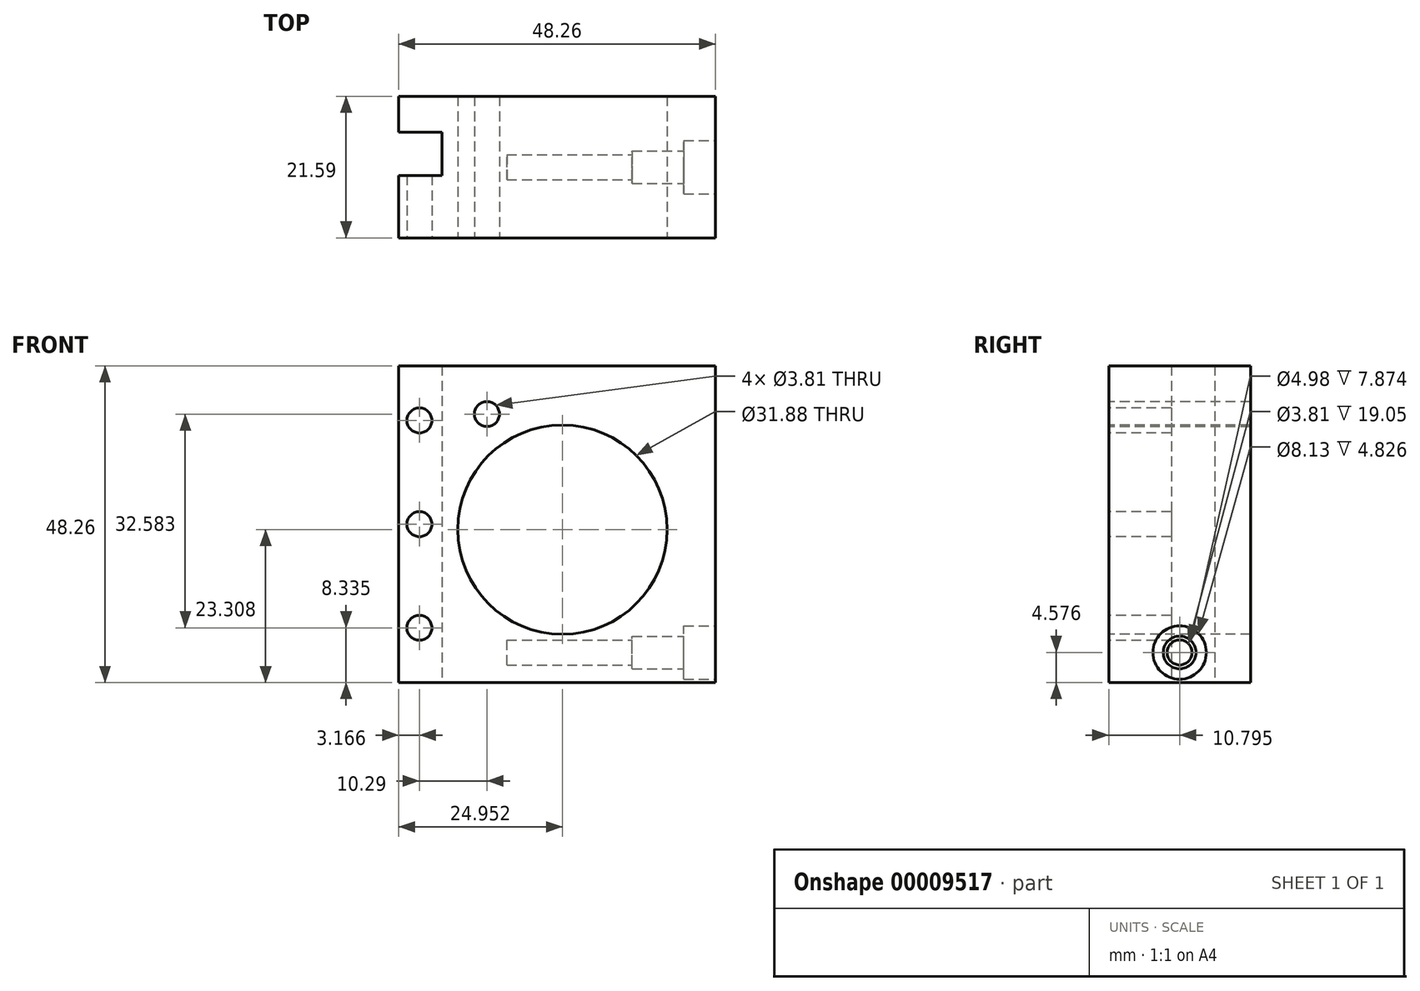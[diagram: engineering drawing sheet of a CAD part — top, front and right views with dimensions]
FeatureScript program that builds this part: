
annotation { "Feature Type Name" : "Feature", "Feature Type Description" : "" }
export const myFeature = defineFeature(function(context is Context, id is Id, definition is map)
    precondition{}
    {
        {
            var Q0;
            Q0=qCreatedBy(makeId("Front.planeOp"),FACE);
            var sketch = newSketch(context, id + "F0", { "sketchPlane" : qUnion([Q0])});
            skLineSegment(sketch, "E0.bottom", {"start": v(-180.25, 28.04) * mm, "end": v(-132, 28.04) * mm});
            skLineSegment(sketch, "E0.top", {"start": v(-180.25, -20.22) * mm, "end": v(-149.6, -20.22) * mm});
            skLineSegment(sketch, "E0.left", {"start": v(-180.25, 28.04) * mm, "end": v(-180.25, -20.22) * mm});
            skLineSegment(sketch, "E0.right", {"start": v(-132, 28.04) * mm, "end": v(-132, -20.22) * mm});
            skCircle(sketch, "E1", {"center": v(-155.3, 3.09) * mm, "radius": 15.94 * mm});
            skLineSegment(sketch, "E2", {"start": v(-155.3, 3.09) * mm, "end": v(-130.34, 3.09) * mm, "construction": true});
            skLineSegment(sketch, "E3", {"start": v(-155.3, 3.09) * mm, "end": v(-155.3, -21.87) * mm, "construction": true});
            skLineSegment(sketch, "E4", {"start": v(-173.65, -20.22) * mm, "end": v(-173.65, 28.04) * mm, "construction": true});
            skLineSegment(sketch, "E5", {"start": v(-177.08, 28.04) * mm, "end": v(-177.08, -20.22) * mm, "construction": true});
            skCircle(sketch, "E6", {"center": v(-177.08, 19.73) * mm, "radius": 1.9 * mm});
            skCircle(sketch, "E7", {"center": v(-177.08, 3.91) * mm, "radius": 1.9 * mm});
            skCircle(sketch, "E8", {"center": v(-177.08, -11.89) * mm, "radius": 1.9 * mm});
            skCircle(sketch, "E9", {"center": v(-166.8, 20.7) * mm, "radius": 1.9 * mm});
            skCircle(sketch, "E10", {"center": v(-155.3, 3.09) * mm, "radius": 4.97 * mm});
            skCircle(sketch, "E11", {"center": v(-155.3, 3.09) * mm, "radius": 7.14 * mm});
            skLineSegment(sketch, "E12.trimOffspring", {"start": v(-146.3, -20.22) * mm, "end": v(-132, -20.22) * mm});
            skCircle(sketch, "E13", {"center": v(-166.8, 20.7) * mm, "radius": 2.45 * mm});
            skLineSegment(sketch, "E14", {"start": v(-149.6, -20.22) * mm, "end": v(-146.3, -20.22) * mm});
            skSolve(sketch);
        }
        {
            var Q0;
            Q0=makeQuery(id+"F0.imprint","IMPRINT",FACE,{"disambiguationData":[TD([[makeQuery(id+"F0.imprint","IMPRINT",EDGE,{"derivedFrom":sQuery(id+"F0.wireOp",EDGE,"E0.bottom")}),-1.0]])]});
            var Q1;
            Q1=makeQuery(id+"F0.imprint","IMPRINT",FACE,{"disambiguationData":[TD([[makeQuery(id+"F0.imprint","IMPRINT",EDGE,{"derivedFrom":sQuery(id+"F0.wireOp",EDGE,"E9")}),1.0]])]});
            var Q2;
            Q2=makeQuery(id+"F0.imprint","IMPRINT",FACE,{"disambiguationData":[TD([[makeQuery(id+"F0.imprint","IMPRINT",EDGE,{"derivedFrom":sQuery(id+"F0.wireOp",EDGE,"E6")}),1.0]])]});
            var Q3;
            Q3=makeQuery(id+"F0.imprint","IMPRINT",FACE,{"disambiguationData":[TD([[makeQuery(id+"F0.imprint","IMPRINT",EDGE,{"derivedFrom":sQuery(id+"F0.wireOp",EDGE,"E7")}),1.0]])]});
            var Q4;
            Q4=makeQuery(id+"F0.imprint","IMPRINT",FACE,{"disambiguationData":[TD([[makeQuery(id+"F0.imprint","IMPRINT",EDGE,{"derivedFrom":sQuery(id+"F0.wireOp",EDGE,"E8")}),1.0]])]});
            var Q5;
            Q5=makeQuery(id+"F0.imprint","IMPRINT",FACE,{"disambiguationData":[TD([[makeQuery(id+"F0.imprint","IMPRINT",EDGE,{"derivedFrom":sQuery(id+"F0.wireOp",EDGE,"E9")}),-1.0]])]});
            var Q6;
            {var subQ1=sQuery(id+"F0.wireOp",EDGE,"2551a94f-3a1d-4b0e-8204-0523b05fb9c7");Q6=makeQuery(id+"F0.imprint","IMPRINT",FACE,{"disambiguationData":[TD([[makeQuery(id+"F0.imprint","IMPRINT",EDGE,{"derivedFrom":subQ1}),1.0]])]});}
            extrude(context, id + "F1", {"entities" : qUnion([Q0, Q1, Q2, Q3, Q4, Q5, Q6]), "oppositeDirection" : true, "depth" : 21.59 * mm});
        }
        {
            var Q0;
            Q0=makeQuery(id+"F0.imprint","IMPRINT",FACE,{"disambiguationData":[TD([[makeQuery(id+"F0.imprint","IMPRINT",EDGE,{"derivedFrom":sQuery(id+"F0.wireOp",EDGE,"E11")}),-1.0]])]});
            var Q1;
            Q1=makeQuery(id+"F0.imprint","IMPRINT",FACE,{"disambiguationData":[TD([[makeQuery(id+"F0.imprint","IMPRINT",EDGE,{"derivedFrom":sQuery(id+"F0.wireOp",EDGE,"E10")}),-1.0]])]});
            var Q2;
            Q2=makeQuery(id+"F0.imprint","IMPRINT",FACE,{"disambiguationData":[TD([[makeQuery(id+"F0.imprint","IMPRINT",EDGE,{"derivedFrom":sQuery(id+"F0.wireOp",EDGE,"E10")}),1.0]])]});
            extrude(context, id + "F2", {"entities" : qUnion([Q0, Q1, Q2]), "oppositeDirection" : true, "depth" : 41.4 * mm});
        }
        {
            var Q0;
            Q0=makeQuery(id+"F0.imprint","IMPRINT",FACE,{"disambiguationData":[TD([[makeQuery(id+"F0.imprint","IMPRINT",EDGE,{"derivedFrom":sQuery(id+"F0.wireOp",EDGE,"E10")}),1.0]])]});
            extrude(context, id + "F3", {"entities" : qUnion([Q0]), "operationType" : NewBodyOperationType.REMOVE, "endBound" : BoundingType.UP_TO_NEXT, "oppositeDirection" : true, "depth" : 25.4 * mm});
        }
        {
            var Q0;
            Q0=makeQuery(id+"F0.imprint","IMPRINT",FACE,{"disambiguationData":[TD([[makeQuery(id+"F0.imprint","IMPRINT",EDGE,{"derivedFrom":sQuery(id+"F0.wireOp",EDGE,"E10")}),-1.0]])]});
            extrude(context, id + "F4", {"entities" : qUnion([Q0]), "operationType" : NewBodyOperationType.REMOVE, "oppositeDirection" : true, "depth" : 3 / 203.2 * mm});
        }
        {
            var Q0;
            Q0=makeQuery(id+"F1.opExtrude","SWEPT_FACE",FACE,{"disambiguationData":[OSD([sQuery(id+"F0.wireOp",EDGE,"E0.top")])]});
            var sketch = newSketch(context, id + "F5", { "sketchPlane" : qUnion([Q0])});
            skLineSegment(sketch, "E15.0", {"start": v(-180.25, -21.59) * mm, "end": v(-180.25, -16.13) * mm, "construction": true});
            skLineSegment(sketch, "E16.0", {"start": v(-180.25, 0) * mm, "end": v(-149.6, 0) * mm, "construction": true});
            skLineSegment(sketch, "E17.0", {"start": v(-180.25, -21.59) * mm, "end": v(-180.25, -21.59) * mm});
            skLineSegment(sketch, "E18.bottom", {"start": v(-180.25, -9.53) * mm, "end": v(-173.65, -9.53) * mm});
            skLineSegment(sketch, "E18.top", {"start": v(-180.25, -16.13) * mm, "end": v(-173.65, -16.13) * mm});
            skLineSegment(sketch, "E18.left", {"start": v(-180.25, -9.53) * mm, "end": v(-180.25, -16.13) * mm});
            skLineSegment(sketch, "E18.right", {"start": v(-173.65, -9.53) * mm, "end": v(-173.65, -16.13) * mm});
            skLineSegment(sketch, "E19", {"start": v(-180.25, -9.53) * mm, "end": v(-180.25, 0) * mm, "construction": true});
            skLineSegment(sketch, "E20", {"start": v(-180.25, -16.13) * mm, "end": v(-180.25, -9.53) * mm, "construction": true});
            skLineSegment(sketch, "E21.0", {"start": v(-132, 0) * mm, "end": v(-132, 0) * mm});
            skLineSegment(sketch, "E22.0", {"start": v(-132, -21.59) * mm, "end": v(-132, -21.59) * mm});
            skLineSegment(sketch, "E23", {"start": v(-136.82, 0) * mm, "end": v(-136.82, -21.59) * mm, "construction": true});
            skLineSegment(sketch, "E24", {"start": v(-163.74, 0) * mm, "end": v(-163.74, -21.59) * mm, "construction": true});
            skLineSegment(sketch, "E25", {"start": v(-162.22, 0) * mm, "end": v(-162.22, -21.59) * mm, "construction": true});
            skSolve(sketch);
        }
        {
            var Q0;
            Q0=makeQuery(id+"F5.imprint","IMPRINT",FACE,{"disambiguationData":[TD([[makeQuery(id+"F5.imprint","IMPRINT",EDGE,{"derivedFrom":sQuery(id+"F5.wireOp",EDGE,"E18.bottom")}),-1.0]])]});
            extrude(context, id + "F6", {"entities" : qUnion([Q0]), "operationType" : NewBodyOperationType.REMOVE, "endBound" : BoundingType.UP_TO_NEXT, "oppositeDirection" : true, "depth" : 25.4 * mm});
        }
        {
            var Q0;
            Q0=makeQuery(id+"F0.imprint","IMPRINT",FACE,{"disambiguationData":[TD([[makeQuery(id+"F0.imprint","IMPRINT",EDGE,{"derivedFrom":sQuery(id+"F0.wireOp",EDGE,"E9")}),1.0]])]});
            extrude(context, id + "F7", {"entities" : qUnion([Q0]), "operationType" : NewBodyOperationType.REMOVE, "endBound" : BoundingType.UP_TO_NEXT, "oppositeDirection" : true, "depth" : 25.4 * mm});
        }
        {
            var Q0;
            Q0=makeQuery(id+"F0.imprint","IMPRINT",FACE,{"disambiguationData":[TD([[makeQuery(id+"F0.imprint","IMPRINT",EDGE,{"derivedFrom":sQuery(id+"F0.wireOp",EDGE,"E6")}),1.0]])]});
            var Q1;
            Q1=makeQuery(id+"F0.imprint","IMPRINT",FACE,{"disambiguationData":[TD([[makeQuery(id+"F0.imprint","IMPRINT",EDGE,{"derivedFrom":sQuery(id+"F0.wireOp",EDGE,"E7")}),1.0]])]});
            var Q2;
            Q2=makeQuery(id+"F0.imprint","IMPRINT",FACE,{"disambiguationData":[TD([[makeQuery(id+"F0.imprint","IMPRINT",EDGE,{"derivedFrom":sQuery(id+"F0.wireOp",EDGE,"E8")}),1.0]])]});
            extrude(context, id + "F8", {"entities" : qUnion([Q0, Q1, Q2]), "operationType" : NewBodyOperationType.REMOVE, "endBound" : BoundingType.UP_TO_NEXT, "oppositeDirection" : true, "depth" : 25.4 * mm});
        }
        {
            var Q0;
            Q0=makeQuery(id+"F1.opExtrude","SWEPT_FACE",FACE,{"disambiguationData":[OSD([sQuery(id+"F0.wireOp",EDGE,"E0.right")])]});
            var sketch = newSketch(context, id + "F9", { "sketchPlane" : qUnion([Q0])});
            skLineSegment(sketch, "E26", {"start": v(12.7, -30.22) * mm, "end": v(12.7, 42.02) * mm, "construction": true});
            skLineSegment(sketch, "E27", {"start": v(0, -15.64) * mm, "end": v(21.59, -15.64) * mm, "construction": true});
            skCircle(sketch, "E28", {"center": v(10.8, -15.64) * mm, "radius": 4.06 * mm});
            skCircle(sketch, "E29", {"center": v(10.8, -15.64) * mm, "radius": 1.9 * mm});
            skCircle(sketch, "E30", {"center": v(10.8, -15.64) * mm, "radius": 2.49 * mm});
            skSolve(sketch);
        }
        {
            var Q0;
            Q0=makeQuery(id+"F9.imprint","IMPRINT",FACE,{"disambiguationData":[TD([[makeQuery(id+"F9.imprint","IMPRINT",EDGE,{"derivedFrom":sQuery(id+"F9.wireOp",EDGE,"E29")}),1.0]])]});
            extrude(context, id + "F10", {"entities" : qUnion([Q0]), "operationType" : NewBodyOperationType.REMOVE, "oppositeDirection" : true, "depth" : 31.75 * mm, "offsetDistance" : 25.4 * mm});
        }
        {
            var Q0;
            Q0=makeQuery(id+"F9.imprint","IMPRINT",FACE,{"disambiguationData":[TD([[makeQuery(id+"F9.imprint","IMPRINT",EDGE,{"derivedFrom":sQuery(id+"F9.wireOp",EDGE,"E29")}),-1.0]])]});
            extrude(context, id + "F11", {"entities" : qUnion([Q0]), "operationType" : NewBodyOperationType.REMOVE, "oppositeDirection" : true, "depth" : 12.7 * mm, "offsetDistance" : 25.4 * mm});
        }
        {
            var Q0;
            Q0=makeQuery(id+"F9.imprint","IMPRINT",FACE,{"disambiguationData":[TD([[makeQuery(id+"F9.imprint","IMPRINT",EDGE,{"derivedFrom":sQuery(id+"F9.wireOp",EDGE,"E28")}),1.0]])]});
            extrude(context, id + "F12", {"entities" : qUnion([Q0]), "operationType" : NewBodyOperationType.REMOVE, "oppositeDirection" : true, "depth" : 4.83 * mm, "offsetDistance" : 25.4 * mm});
        }
        {
            var Q0;
            Q0=makeQuery(id+"F2.opExtrude","SWEPT_BODY",BODY,{"disambiguationData":[OSD([sQuery(id+"F0.wireOp",EDGE,"E1")])]});
            deleteBodies(context, id + "F13", {"entities" : qUnion([Q0])});
        }
    });
